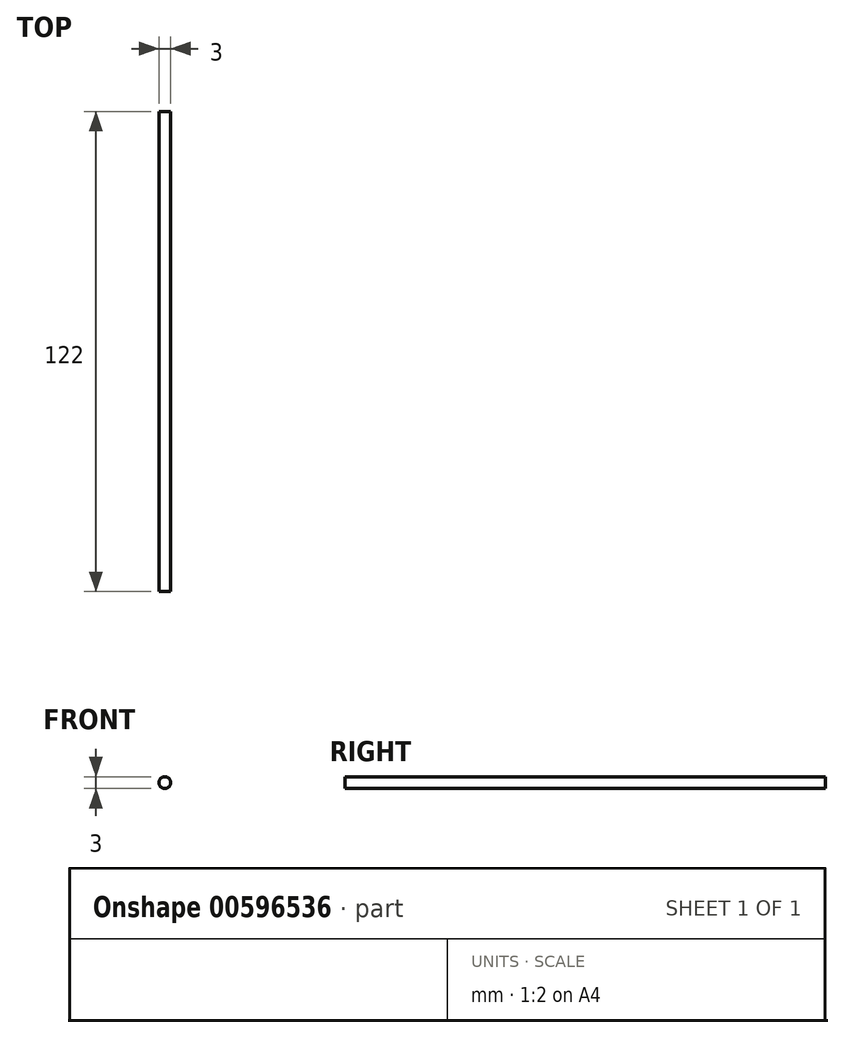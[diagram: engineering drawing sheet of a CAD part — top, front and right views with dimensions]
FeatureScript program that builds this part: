
annotation { "Feature Type Name" : "Feature", "Feature Type Description" : "" }
export const myFeature = defineFeature(function(context is Context, id is Id, definition is map)
    precondition{}
    {
        {
            var Q0;
            Q0=qCreatedBy(makeId("Front.planeOp"),FACE);
            var sketch = newSketch(context, id + "F0", { "sketchPlane" : qUnion([Q0])});
            skCircle(sketch, "E0", {"center": v(0, 0) * mm, "radius": 1.5 * mm});
            skSolve(sketch);
        }
        {
            var Q0;
            Q0=makeQuery(id+"F0.imprint","IMPRINT",FACE,{"disambiguationData":[TD([[makeQuery(id+"F0.imprint","IMPRINT",EDGE,{"derivedFrom":sQuery(id+"F0.wireOp",EDGE,"E0")}),1.0]])]});
            extrude(context, id + "F1", {"entities" : qUnion([Q0]), "depth" : 122 * mm, "offsetDistance" : 25 * mm});
        }
    });
